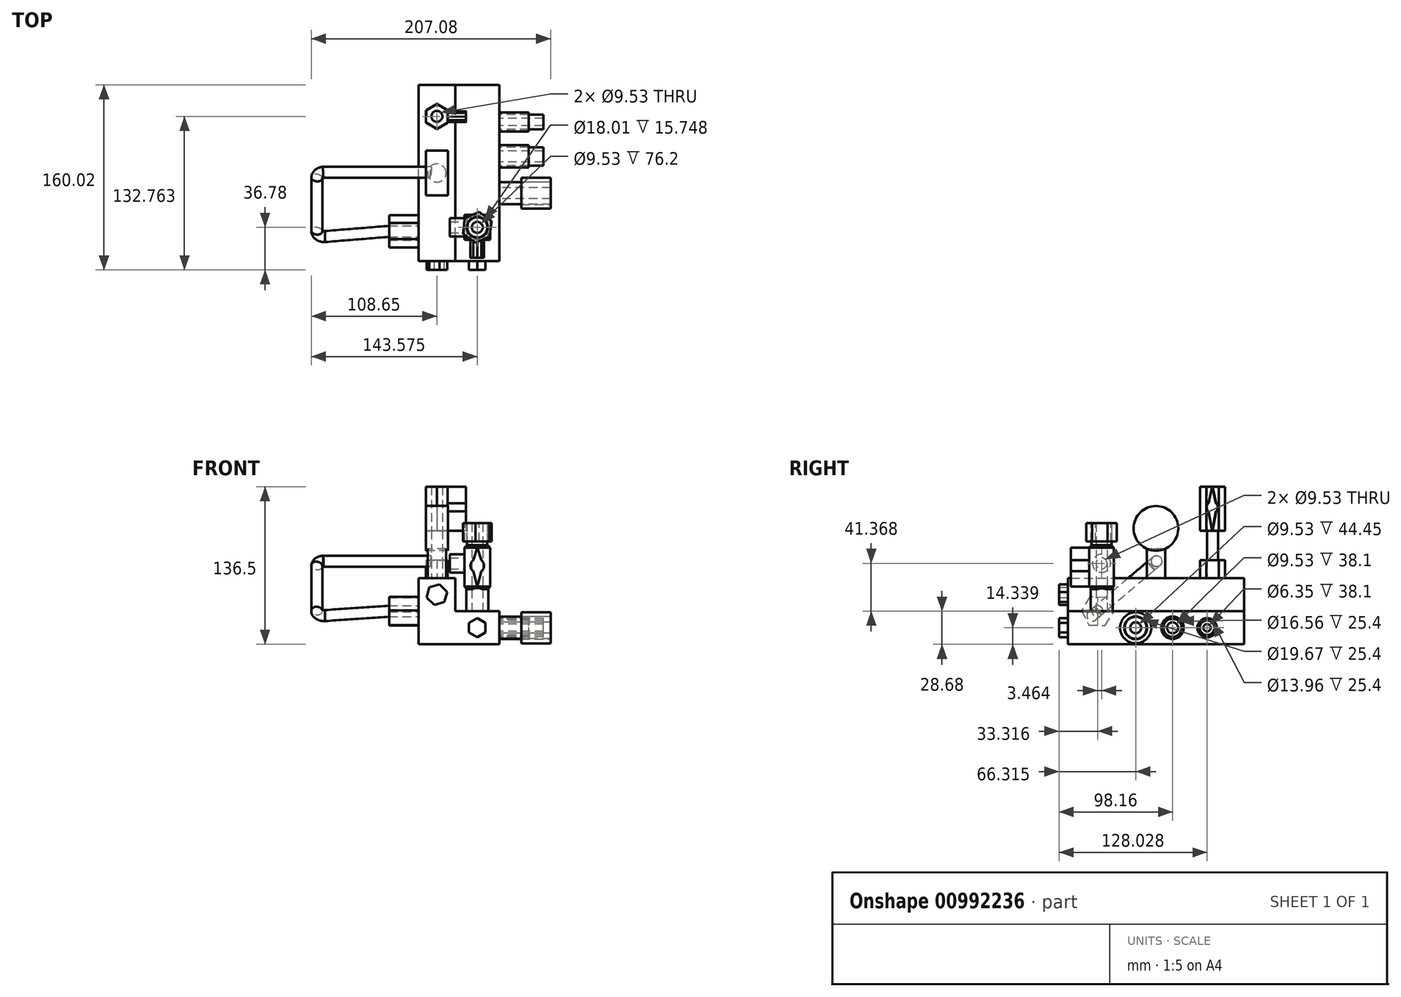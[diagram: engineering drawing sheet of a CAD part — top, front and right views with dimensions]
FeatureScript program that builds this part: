
annotation { "Feature Type Name" : "Feature", "Feature Type Description" : "" }
export const myFeature = defineFeature(function(context is Context, id is Id, definition is map)
    precondition{}
    {
        {
            var Q0;
            Q0=qCreatedBy(makeId("Front.planeOp"),FACE);
            var sketch = newSketch(context, id + "F0", { "sketchPlane" : qUnion([Q0])});
            skLineSegment(sketch, "E0.bottom", {"start": v(15.87, -28.57) * mm, "end": v(-15.88, -28.58) * mm});
            skLineSegment(sketch, "E0.top", {"start": v(15.88, 28.58) * mm, "end": v(-15.88, 28.57) * mm});
            skLineSegment(sketch, "E0.left", {"start": v(15.87, 0) * mm, "end": v(15.88, 28.58) * mm});
            skLineSegment(sketch, "E0.right", {"start": v(-15.88, -28.58) * mm, "end": v(-15.88, 28.57) * mm});
            skPoint(sketch, "E0.middle", {"position": v(0, 0) * mm});
            skLineSegment(sketch, "E1.bottom", {"start": v(15.87, 0) * mm, "end": v(53.97, 0) * mm});
            skLineSegment(sketch, "E1.top", {"start": v(15.87, -28.68) * mm, "end": v(53.97, -28.68) * mm});
            skLineSegment(sketch, "E1.left", {"start": v(15.87, -28.58) * mm, "end": v(15.87, -28.68) * mm});
            skLineSegment(sketch, "E1.right", {"start": v(53.97, 0) * mm, "end": v(53.97, -28.68) * mm});
            skSolve(sketch);
        }
        {
            var Q0;
            Q0 = qSketchRegion(id + "F0", true);
            extrude(context, id + "F1", {"entities" : qUnion([Q0]), "endBound" : BoundingType.SYMMETRIC, "depth" : 152.4 * mm, "offsetDistance" : 25.4 * mm});
        }
        {
            var Q0;
            Q0=makeQuery(id+"F1.opExtrude","SWEPT_FACE",FACE,{"disambiguationData":[OSD([sQuery(id+"F0.wireOp",EDGE,"E1.right")])]});
            var sketch = newSketch(context, id + "F2", { "sketchPlane" : qUnion([Q0])});
            skCircle(sketch, "E2", {"center": v(-17.5, -14.34) * mm, "radius": 9.53 * mm});
            skPoint(sketch, "E2.centerSnap0", {"position": v(-76.2, -14.34) * mm});
            skCircle(sketch, "E3", {"center": v(-17.5, -14.34) * mm, "radius": 4.76 * mm});
            skSolve(sketch);
        }
        {
            var Q0;
            Q0 = qSketchRegion(id + "F2", true);
            extrude(context, id + "F3", {"entities" : qUnion([Q0]), "operationType" : NewBodyOperationType.ADD, "depth" : 44.45 * mm, "offsetDistance" : 25.4 * mm});
        }
        {
            var Q0;
            {var subQ1=sQuery(id+"F0.wireOp",EDGE,"E1.right");var subQ3=sQuery(id+"F0.wireOp",EDGE,"E1.bottom");Q0=makeQuery(id+"F3.boolean.opBoolean","SPLIT",FACE,{"disambiguationData":[TD([makeQuery(id+"F1.opExtrude","SWEPT_FACE",FACE,{"disambiguationData":[OSD([subQ3])]})])],"derivedFrom":makeQuery(id+"F1.opExtrude","SWEPT_FACE",FACE,{"disambiguationData":[OSD([subQ1])]})});}
            var sketch = newSketch(context, id + "F4", { "sketchPlane" : qUnion([Q0])});
            skCircle(sketch, "E4", {"center": v(14.34, -14.34) * mm, "radius": 7.87 * mm});
            skPoint(sketch, "E4.centerSnap0", {"position": v(-76.2, -14.34) * mm});
            skCircle(sketch, "E5", {"center": v(14.34, -14.34) * mm, "radius": 4.76 * mm});
            skCircle(sketch, "E6", {"center": v(44.2, -14.34) * mm, "radius": 6.35 * mm});
            skCircle(sketch, "E7", {"center": v(44.2, -14.34) * mm, "radius": 3.18 * mm});
            skSolve(sketch);
        }
        {
            var Q0;
            Q0 = qSketchRegion(id + "F4", true);
            extrude(context, id + "F5", {"entities" : qUnion([Q0]), "operationType" : NewBodyOperationType.ADD, "depth" : 38.1 * mm, "offsetDistance" : 25.4 * mm});
        }
        {
            var Q0;
            Q0=makeQuery(id+"F3.opExtrude","CAP_FACE",FACE,{"disambiguationData":[OSD([sQuery(id+"F2.wireOp",EDGE,"E2"),sQuery(id+"F2.wireOp",EDGE,"E3")])],"isStart":false});
            var sketch = newSketch(context, id + "F6", { "sketchPlane" : qUnion([Q0])});
            skCircle(sketch, "E8", {"center": v(-17.5, -14.34) * mm, "radius": 9.84 * mm});
            skCircle(sketch, "E9", {"center": v(-17.5, -14.34) * mm, "radius": 13.46 * mm});
            skSolve(sketch);
        }
        {
            var Q0;
            Q0 = qSketchRegion(id + "F6", true);
            extrude(context, id + "F7", {"entities" : qUnion([Q0]), "oppositeDirection" : true, "depth" : 25.4 * mm, "offsetDistance" : 25.4 * mm});
        }
        {
            var Q0;
            {var subQ2=sQuery(id+"F0.wireOp",EDGE,"E1.right");var subQ4=sQuery(id+"F0.wireOp",EDGE,"E1.bottom");var subQ10=makeQuery(id+"F1.opExtrude","SWEPT_FACE",FACE,{"disambiguationData":[OSD([subQ4])]});Q0=makeQuery(id+"F5.boolean.opBoolean","SPLIT",FACE,{"disambiguationData":[TD([subQ10])],"derivedFrom":makeQuery(id+"F3.boolean.opBoolean","SPLIT",FACE,{"disambiguationData":[TD([subQ10])],"derivedFrom":makeQuery(id+"F1.opExtrude","SWEPT_FACE",FACE,{"disambiguationData":[OSD([subQ2])]})})});}
            var sketch = newSketch(context, id + "F8", { "sketchPlane" : qUnion([Q0])});
            skCircle(sketch, "E10", {"center": v(14.34, -14.34) * mm, "radius": 8.28 * mm});
            skCircle(sketch, "E11", {"center": v(14.34, -14.34) * mm, "radius": 9.67 * mm});
            skCircle(sketch, "E12", {"center": v(44.2, -14.34) * mm, "radius": 6.98 * mm});
            skCircle(sketch, "E13", {"center": v(44.2, -14.34) * mm, "radius": 8.3 * mm});
            skSolve(sketch);
        }
        {
            var Q0;
            Q0 = qSketchRegion(id + "F8", true);
            extrude(context, id + "F9", {"entities" : qUnion([Q0]), "depth" : 25.4 * mm, "offsetDistance" : 25.4 * mm});
        }
        {
            var Q0;
            Q0=makeQuery(id+"F1.opExtrude","SWEPT_FACE",FACE,{"disambiguationData":[OSD([sQuery(id+"F0.wireOp",EDGE,"E1.bottom")])]});
            var sketch = newSketch(context, id + "F10", { "sketchPlane" : qUnion([Q0])});
            skCircle(sketch, "E14", {"center": v(34.92, -47.04) * mm, "radius": 9.53 * mm});
            skPoint(sketch, "E14.centerSnap0", {"position": v(34.92, -76.2) * mm});
            skCircle(sketch, "E15", {"center": v(34.92, -47.04) * mm, "radius": 4.76 * mm});
            skSolve(sketch);
        }
        {
            var Q0;
            Q0 = qSketchRegion(id + "F10", true);
            extrude(context, id + "F11", {"entities" : qUnion([Q0]), "operationType" : NewBodyOperationType.ADD, "depth" : 19.05 * mm, "offsetDistance" : 25.4 * mm});
        }
        {
            var Q0;
            Q0=makeQuery(id+"F11.opExtrude","CAP_FACE",FACE,{"disambiguationData":[OSD([sQuery(id+"F10.wireOp",EDGE,"E14"),sQuery(id+"F10.wireOp",EDGE,"E15")])],"isStart":false});
            var sketch = newSketch(context, id + "F12", { "sketchPlane" : qUnion([Q0])});
            skLineSegment(sketch, "E16.bottom", {"start": v(46.02, -57.76) * mm, "end": v(23.83, -57.76) * mm});
            skLineSegment(sketch, "E16.top", {"start": v(46.02, -36.32) * mm, "end": v(23.83, -36.32) * mm});
            skLineSegment(sketch, "E16.left", {"start": v(46.02, -57.76) * mm, "end": v(46.02, -36.32) * mm});
            skLineSegment(sketch, "E16.right", {"start": v(23.83, -57.76) * mm, "end": v(23.83, -36.32) * mm});
            skPoint(sketch, "E16.middle", {"position": v(34.92, -47.04) * mm});
            skCircle(sketch, "E17", {"center": v(34.92, -47.04) * mm, "radius": 4.76 * mm});
            skSolve(sketch);
        }
        {
            var Q0;
            Q0 = qSketchRegion(id + "F12", true);
            extrude(context, id + "F13", {"entities" : qUnion([Q0]), "operationType" : NewBodyOperationType.ADD, "depth" : 38.1 * mm, "offsetDistance" : 25.4 * mm});
        }
        {
            var Q0;
            Q0=makeQuery(id+"F13.opExtrude","CAP_EDGE",EDGE,{"disambiguationData":[OSD([sQuery(id+"F12.wireOp",EDGE,"E16.right")])],"isStart":false});
            var Q1;
            Q1=makeQuery(id+"F13.opExtrude","CAP_EDGE",EDGE,{"disambiguationData":[OSD([sQuery(id+"F12.wireOp",EDGE,"E16.bottom")])],"isStart":false});
            var Q2;
            Q2=makeQuery(id+"F13.opExtrude","CAP_EDGE",EDGE,{"disambiguationData":[OSD([sQuery(id+"F12.wireOp",EDGE,"E16.left")])],"isStart":false});
            var Q3;
            Q3=makeQuery(id+"F13.opExtrude","CAP_EDGE",EDGE,{"disambiguationData":[OSD([sQuery(id+"F12.wireOp",EDGE,"E16.top")])],"isStart":false});
            var Q4;
            Q4=makeQuery(id+"F13.opExtrude","CAP_EDGE",EDGE,{"disambiguationData":[OSD([sQuery(id+"F12.wireOp",EDGE,"E16.bottom")])],"isStart":true});
            var Q5;
            Q5=makeQuery(id+"F13.opExtrude","CAP_EDGE",EDGE,{"disambiguationData":[OSD([sQuery(id+"F12.wireOp",EDGE,"E16.left")])],"isStart":true});
            var Q6;
            Q6=makeQuery(id+"F13.opExtrude","CAP_EDGE",EDGE,{"disambiguationData":[OSD([sQuery(id+"F12.wireOp",EDGE,"E16.top")])],"isStart":true});
            var Q7;
            Q7=makeQuery(id+"F13.opExtrude","CAP_EDGE",EDGE,{"disambiguationData":[OSD([sQuery(id+"F12.wireOp",EDGE,"E16.right")])],"isStart":true});
            chamfer(context, id + "F14", {"entities" : qUnion([Q0, Q1, Q2, Q3, Q4, Q5, Q6, Q7]), "width" : 2.3 * mm, "tangentPropagation" : true});
        }
        {
            var Q0;
            Q0=makeQuery(id+"F13.opExtrude","CAP_FACE",FACE,{"disambiguationData":[OSD([sQuery(id+"F12.wireOp",EDGE,"E16.bottom"),sQuery(id+"F12.wireOp",EDGE,"E16.top"),sQuery(id+"F12.wireOp",EDGE,"E16.left"),sQuery(id+"F12.wireOp",EDGE,"E16.right"),sQuery(id+"F12.wireOp",EDGE,"E17")])],"isStart":false});
            var sketch = newSketch(context, id + "F15", { "sketchPlane" : qUnion([Q0])});
            skCircle(sketch, "E18", {"center": v(34.92, -47.04) * mm, "radius": 8.73 * mm});
            skCircle(sketch, "E19", {"center": v(34.92, -47.04) * mm, "radius": 4.76 * mm});
            skSolve(sketch);
        }
        {
            var Q0;
            Q0 = qSketchRegion(id + "F15", true);
            extrude(context, id + "F16", {"entities" : qUnion([Q0]), "operationType" : NewBodyOperationType.ADD, "depth" : 19.05 * mm, "offsetDistance" : 25.4 * mm});
        }
        {
            var Q0;
            Q0=makeQuery(id+"F16.opExtrude","CAP_FACE",FACE,{"disambiguationData":[OSD([sQuery(id+"F15.wireOp",EDGE,"E18"),sQuery(id+"F15.wireOp",EDGE,"E19")])],"isStart":false});
            var sketch = newSketch(context, id + "F17", { "sketchPlane" : qUnion([Q0])});
            skCircle(sketch, "E20", {"center": v(34.92, -47.04) * mm, "radius": 9 * mm});
            skCircle(sketch, "E21.cCircle", {"center": v(34.92, -47.04) * mm, "radius": 11.58 * mm, "construction": true});
            skLineSegment(sketch, "E21.0", {"start": v(47.24, -41.82) * mm, "end": v(45.6, -55.1) * mm});
            skLineSegment(sketch, "E21.1", {"start": v(45.6, -55.1) * mm, "end": v(33.28, -60.31) * mm});
            skLineSegment(sketch, "E21.2", {"start": v(33.28, -60.31) * mm, "end": v(22.6, -52.26) * mm});
            skLineSegment(sketch, "E21.3", {"start": v(22.6, -52.26) * mm, "end": v(24.25, -38.98) * mm});
            skLineSegment(sketch, "E21.4", {"start": v(24.25, -38.98) * mm, "end": v(36.57, -33.77) * mm});
            skLineSegment(sketch, "E21.5", {"start": v(36.57, -33.77) * mm, "end": v(47.24, -41.82) * mm});
            skPoint(sketch, "E21.0.midPoint", {"position": v(46.42, -48.46) * mm});
            skSolve(sketch);
        }
        {
            var Q0;
            Q0 = qSketchRegion(id + "F17", true);
            extrude(context, id + "F18", {"entities" : qUnion([Q0]), "oppositeDirection" : true, "depth" : 15.75 * mm, "offsetDistance" : 25.4 * mm});
        }
        {
            var Q0;
            Q0=makeQuery(id+"F13.opExtrude","SWEPT_FACE",FACE,{"disambiguationData":[OSD([sQuery(id+"F12.wireOp",EDGE,"E16.bottom")])]});
            var sketch = newSketch(context, id + "F19", { "sketchPlane" : qUnion([Q0])});
            skCircle(sketch, "E22", {"center": v(34.92, 39.36) * mm, "radius": 5.92 * mm});
            skPoint(sketch, "E22.centerSnap0", {"position": v(34.92, 54.86) * mm});
            skLineSegment(sketch, "E23", {"start": v(34.92, 54.86) * mm, "end": v(34.92, 21.34) * mm, "construction": true});
            skLineSegment(sketch, "E24", {"start": v(31.51, 44.2) * mm, "end": v(34.92, 54.86) * mm});
            skLineSegment(sketch, "E25", {"start": v(31.51, 34.52) * mm, "end": v(34.92, 21.34) * mm});
            skLineSegment(sketch, "E26.MirrorCS", {"start": v(38.34, 44.2) * mm, "end": v(34.92, 54.86) * mm});
            skLineSegment(sketch, "E27.MirrorCS", {"start": v(38.34, 34.52) * mm, "end": v(34.92, 21.34) * mm});
            skSolve(sketch);
        }
        {
            var Q0;
            Q0 = qSketchRegion(id + "F19", true);
            extrude(context, id + "F20", {"entities" : qUnion([Q0]), "depth" : 15.75 * mm, "offsetDistance" : 25.4 * mm});
        }
        {
            var Q0;
            Q0=makeQuery(id+"F1.opExtrude","CAP_FACE",FACE,{"disambiguationData":[OSD([sQuery(id+"F0.wireOp",EDGE,"E0.bottom"),sQuery(id+"F0.wireOp",EDGE,"E0.top"),sQuery(id+"F0.wireOp",EDGE,"E0.left"),sQuery(id+"F0.wireOp",EDGE,"E0.right"),sQuery(id+"F0.wireOp",EDGE,"E1.bottom"),sQuery(id+"F0.wireOp",EDGE,"E1.top"),sQuery(id+"F0.wireOp",EDGE,"E1.left"),sQuery(id+"F0.wireOp",EDGE,"E1.right")])],"isStart":false});
            var sketch = newSketch(context, id + "F21", { "sketchPlane" : qUnion([Q0])});
            skCircle(sketch, "E28.cCircle", {"center": v(34.92, -14.34) * mm, "radius": 7.14 * mm, "construction": true});
            skPoint(sketch, "E28.cCircle.centerSnap0", {"position": v(53.97, -14.34) * mm});
            skPoint(sketch, "E28.cCircle.centerSnap1", {"position": v(34.92, 0) * mm});
            skLineSegment(sketch, "E28.0", {"start": v(42.07, -10.22) * mm, "end": v(42.07, -18.46) * mm});
            skLineSegment(sketch, "E28.1", {"start": v(42.07, -18.46) * mm, "end": v(34.92, -22.59) * mm});
            skLineSegment(sketch, "E28.2", {"start": v(34.92, -22.59) * mm, "end": v(27.78, -18.46) * mm});
            skLineSegment(sketch, "E28.3", {"start": v(27.78, -18.46) * mm, "end": v(27.78, -10.22) * mm});
            skLineSegment(sketch, "E28.4", {"start": v(27.78, -10.22) * mm, "end": v(34.92, -6.1) * mm});
            skLineSegment(sketch, "E28.5", {"start": v(34.92, -6.1) * mm, "end": v(42.07, -10.22) * mm});
            skPoint(sketch, "E28.0.midPoint", {"position": v(42.07, -14.34) * mm});
            skCircle(sketch, "E29.cCircle", {"center": v(0, 14.29) * mm, "radius": 7.91 * mm, "construction": true});
            skPoint(sketch, "E29.cCircle.centerSnap0", {"position": v(15.87, 14.29) * mm});
            skPoint(sketch, "E29.cCircle.centerSnap1", {"position": v(0, 28.58) * mm});
            skLineSegment(sketch, "E29.0", {"start": v(8.82, 16.68) * mm, "end": v(6.48, 7.85) * mm});
            skLineSegment(sketch, "E29.1", {"start": v(6.48, 7.85) * mm, "end": v(-2.34, 5.45) * mm});
            skLineSegment(sketch, "E29.2", {"start": v(-2.34, 5.45) * mm, "end": v(-8.82, 11.9) * mm});
            skLineSegment(sketch, "E29.3", {"start": v(-8.82, 11.9) * mm, "end": v(-6.48, 20.73) * mm});
            skLineSegment(sketch, "E29.4", {"start": v(-6.48, 20.73) * mm, "end": v(2.34, 23.12) * mm});
            skLineSegment(sketch, "E29.5", {"start": v(2.34, 23.12) * mm, "end": v(8.82, 16.68) * mm});
            skPoint(sketch, "E29.0.midPoint", {"position": v(7.65, 12.26) * mm});
            skSolve(sketch);
        }
        {
            var Q0;
            Q0 = qSketchRegion(id + "F21", true);
            extrude(context, id + "F22", {"entities" : qUnion([Q0]), "depth" : 7.62 * mm, "offsetDistance" : 25.4 * mm});
        }
        {
            var Q0;
            Q0=makeQuery(id+"F1.opExtrude","SWEPT_FACE",FACE,{"disambiguationData":[OSD([sQuery(id+"F0.wireOp",EDGE,"E0.top")])]});
            var sketch = newSketch(context, id + "F23", { "sketchPlane" : qUnion([Q0])});
            skCircle(sketch, "E30", {"center": v(0, 0) * mm, "radius": 7.87 * mm});
            skSolve(sketch);
        }
        {
            var Q0;
            Q0 = qSketchRegion(id + "F23", true);
            extrude(context, id + "F24", {"entities" : qUnion([Q0]), "depth" : 25.4 * mm, "offsetDistance" : 25.4 * mm});
        }
        {
            var Q0;
            Q0=qCreatedBy(makeId("Right.planeOp"),FACE);
            var sketch = newSketch(context, id + "F25", { "sketchPlane" : qUnion([Q0])});
            skCircle(sketch, "E31", {"center": v(0, 71.65) * mm, "radius": 19.36 * mm});
            skSolve(sketch);
        }
        {
            var Q0;
            Q0 = qSketchRegion(id + "F25", true);
            extrude(context, id + "F26", {"entities" : qUnion([Q0]), "endBound" : BoundingType.SYMMETRIC, "depth" : 19.05 * mm, "offsetDistance" : 25.4 * mm});
        }
        {
            var Q0;
            Q0=makeQuery(id+"F1.opExtrude","SWEPT_FACE",FACE,{"disambiguationData":[OSD([sQuery(id+"F0.wireOp",EDGE,"E0.top")])]});
            var sketch = newSketch(context, id + "F27", { "sketchPlane" : qUnion([Q0])});
            skCircle(sketch, "E32.cCircle", {"center": v(0, 48.94) * mm, "radius": 9.35 * mm, "construction": true});
            skLineSegment(sketch, "E32.0", {"start": v(9.35, 54.34) * mm, "end": v(9.35, 43.55) * mm});
            skLineSegment(sketch, "E32.1", {"start": v(9.35, 43.55) * mm, "end": v(0, 38.15) * mm});
            skLineSegment(sketch, "E32.2", {"start": v(0, 38.15) * mm, "end": v(-9.35, 43.55) * mm});
            skLineSegment(sketch, "E32.3", {"start": v(-9.35, 43.55) * mm, "end": v(-9.35, 54.34) * mm});
            skLineSegment(sketch, "E32.4", {"start": v(-9.35, 54.34) * mm, "end": v(0, 59.74) * mm});
            skLineSegment(sketch, "E32.5", {"start": v(0, 59.74) * mm, "end": v(9.35, 54.34) * mm});
            skPoint(sketch, "E32.0.midPoint", {"position": v(9.35, 48.94) * mm});
            skCircle(sketch, "E33", {"center": v(0, 48.94) * mm, "radius": 4.76 * mm});
            skSolve(sketch);
        }
        {
            var Q0;
            Q0 = qSketchRegion(id + "F27", true);
            extrude(context, id + "F28", {"entities" : qUnion([Q0]), "depth" : 15.75 * mm, "offsetDistance" : 25.4 * mm});
        }
        {
            var Q0;
            Q0=makeQuery(id+"F28.opExtrude","CAP_FACE",FACE,{"disambiguationData":[OSD([sQuery(id+"F27.wireOp",EDGE,"E32.0"),sQuery(id+"F27.wireOp",EDGE,"E32.1"),sQuery(id+"F27.wireOp",EDGE,"E32.2"),sQuery(id+"F27.wireOp",EDGE,"E32.3"),sQuery(id+"F27.wireOp",EDGE,"E32.4"),sQuery(id+"F27.wireOp",EDGE,"E32.5"),sQuery(id+"F27.wireOp",EDGE,"E33")])],"isStart":false});
            var sketch = newSketch(context, id + "F29", { "sketchPlane" : qUnion([Q0])});
            skCircle(sketch, "E34", {"center": v(0, 48.94) * mm, "radius": 4.76 * mm});
            skSolve(sketch);
        }
        {
            var Q0;
            Q0 = qSketchRegion(id + "F29", true);
            extrude(context, id + "F30", {"entities" : qUnion([Q0]), "depth" : 25.4 * mm, "offsetDistance" : 25.4 * mm});
        }
        {
            var Q0;
            Q0=makeQuery(id+"F30.opExtrude","CAP_FACE",FACE,{"disambiguationData":[OSD([sQuery(id+"F29.wireOp",EDGE,"E34")])],"isStart":false});
            var sketch = newSketch(context, id + "F31", { "sketchPlane" : qUnion([Q0])});
            skCircle(sketch, "E35.cCircle", {"center": v(0, 48.94) * mm, "radius": 9.3 * mm, "construction": true});
            skLineSegment(sketch, "E35.0", {"start": v(9.25, 43.48) * mm, "end": v(-0.1, 38.2) * mm});
            skLineSegment(sketch, "E35.1", {"start": v(-0.1, 38.2) * mm, "end": v(-9.35, 43.67) * mm});
            skLineSegment(sketch, "E35.2", {"start": v(-9.35, 43.67) * mm, "end": v(-9.25, 54.4) * mm});
            skLineSegment(sketch, "E35.3", {"start": v(-9.25, 54.4) * mm, "end": v(0.1, 59.68) * mm});
            skLineSegment(sketch, "E35.4", {"start": v(0.1, 59.68) * mm, "end": v(9.35, 54.22) * mm});
            skLineSegment(sketch, "E35.5", {"start": v(9.35, 54.22) * mm, "end": v(9.25, 43.48) * mm});
            skPoint(sketch, "E35.0.midPoint", {"position": v(4.57, 40.84) * mm});
            skCircle(sketch, "E36", {"center": v(0, 48.94) * mm, "radius": 4.76 * mm});
            skSolve(sketch);
        }
        {
            var Q0;
            Q0 = qSketchRegion(id + "F31", true);
            extrude(context, id + "F32", {"entities" : qUnion([Q0]), "depth" : 38.1 * mm, "offsetDistance" : 25.4 * mm});
        }
        {
            var Q0;
            Q0=makeQuery(id+"F32.opExtrude","SWEPT_FACE",FACE,{"disambiguationData":[OSD([sQuery(id+"F31.wireOp",EDGE,"E35.5")])]});
            var sketch = newSketch(context, id + "F33", { "sketchPlane" : qUnion([Q0])});
            skCircle(sketch, "E37", {"center": v(48.94, 89.85) * mm, "radius": 4.78 * mm});
            skPoint(sketch, "E37.centerSnap0", {"position": v(48.94, 107.82) * mm});
            skLineSegment(sketch, "E38", {"start": v(48.94, 107.82) * mm, "end": v(48.94, 69.72) * mm, "construction": true});
            skLineSegment(sketch, "E39", {"start": v(45.81, 93.47) * mm, "end": v(48.94, 107.82) * mm});
            skLineSegment(sketch, "E40", {"start": v(45.81, 86.24) * mm, "end": v(48.94, 69.72) * mm});
            skLineSegment(sketch, "E41.MirrorCS", {"start": v(52.07, 93.47) * mm, "end": v(48.94, 107.82) * mm});
            skLineSegment(sketch, "E42.MirrorCS", {"start": v(52.07, 86.24) * mm, "end": v(48.94, 69.72) * mm});
            skSolve(sketch);
        }
        {
            var Q0;
            Q0 = qSketchRegion(id + "F33", true);
            extrude(context, id + "F34", {"entities" : qUnion([Q0]), "depth" : 15.75 * mm, "offsetDistance" : 25.4 * mm});
        }
        {
            var Q0;
            Q0=makeQuery(id+"F1.opExtrude","SWEPT_FACE",FACE,{"disambiguationData":[OSD([sQuery(id+"F0.wireOp",EDGE,"E0.right")])]});
            var sketch = newSketch(context, id + "F35", { "sketchPlane" : qUnion([Q0])});
            skCircle(sketch, "E43.cCircle", {"center": v(50.5, 0) * mm, "radius": 12.16 * mm, "construction": true});
            skLineSegment(sketch, "E43.0", {"start": v(64.53, 0.52) * mm, "end": v(57.97, -11.89) * mm});
            skLineSegment(sketch, "E43.1", {"start": v(57.97, -11.89) * mm, "end": v(43.94, -12.41) * mm});
            skLineSegment(sketch, "E43.2", {"start": v(43.94, -12.41) * mm, "end": v(36.47, -0.52) * mm});
            skLineSegment(sketch, "E43.3", {"start": v(36.47, -0.52) * mm, "end": v(43.04, 11.89) * mm});
            skLineSegment(sketch, "E43.4", {"start": v(43.04, 11.89) * mm, "end": v(57.07, 12.41) * mm});
            skLineSegment(sketch, "E43.5", {"start": v(57.07, 12.41) * mm, "end": v(64.53, 0.52) * mm});
            skPoint(sketch, "E43.0.midPoint", {"position": v(61.25, -5.68) * mm});
            skCircle(sketch, "E44", {"center": v(50.5, 0) * mm, "radius": 4.76 * mm});
            skSolve(sketch);
        }
        {
            var Q0;
            Q0 = qSketchRegion(id + "F35", true);
            extrude(context, id + "F36", {"entities" : qUnion([Q0]), "depth" : 25.4 * mm, "offsetDistance" : 25.4 * mm});
        }
        {
            var Q0;
            Q0=makeQuery(id+"F36.opExtrude","CAP_FACE",FACE,{"disambiguationData":[OSD([sQuery(id+"F35.wireOp",EDGE,"E43.0"),sQuery(id+"F35.wireOp",EDGE,"E43.1"),sQuery(id+"F35.wireOp",EDGE,"E43.2"),sQuery(id+"F35.wireOp",EDGE,"E43.3"),sQuery(id+"F35.wireOp",EDGE,"E43.4"),sQuery(id+"F35.wireOp",EDGE,"E43.5"),sQuery(id+"F35.wireOp",EDGE,"E44")])],"isStart":false});
            var sketch = newSketch(context, id + "F37", { "sketchPlane" : qUnion([Q0])});
            skPoint(sketch, "E45.center.orphan", {"position": v(50.5, 0) * mm});
            skPoint(sketch, "E46", {"position": v(0, 42.8) * mm});
            skLineSegment(sketch, "E47", {"start": v(0, 42.8) * mm, "end": v(50.5, 0) * mm, "construction": true});
            skSolve(sketch);
        }
        {
            var Q0;
            Q0=sQuery(id+"F37.wireOp",EDGE,"E47");
            cPlane(context, id + "F38", {"entities" : qUnion([Q0]), "cplaneType" : CPlaneType.LINE_ANGLE, "offset" : 25.4 * mm, "angle" : 0 * degree, "width" : 152.4 * mm, "height" : 152.4 * mm});
        }
        {
            var Q0;
            Q0=qCreatedBy(id+"F38.planeOp",FACE);
            var sketch = newSketch(context, id + "F39", { "sketchPlane" : qUnion([Q0])});
            skLineSegment(sketch, "E48", {"start": v(-41.18, 38.57) * mm, "end": v(-96.94, 44.45) * mm});
            skLineSegment(sketch, "E49", {"start": v(-103.95, 38.13) * mm, "end": v(-103.95, -22.2) * mm});
            skPoint(sketch, "E50.visualSharp", {"position": v(-103.95, 45.18) * mm});
            skArc(sketch, "E50.filletArc", {"start": v(-96.94, 44.45) * mm, "mid": v(-101.85, 42.85) * mm, "end": v(-103.95, 38.13) * mm});
            skPoint(sketch, "E51.visualSharp", {"position": v(-103.95, -27.92) * mm});
            skArc(sketch, "E51.filletArc", {"start": v(-103.95, -22.2) * mm, "mid": v(-102.32, -26.45) * mm, "end": v(-98.27, -28.52) * mm});
            skPoint(sketch, "E52.end.orphan", {"position": v(0, -38.88) * mm});
            skLineSegment(sketch, "E53", {"start": v(-98.27, -28.52) * mm, "end": v(-5.32, -28.52) * mm});
            skSolve(sketch);
        }
        {
            var Q0;
            Q0=makeQuery(id+"F37.imprint","IMPRINT",FACE,{"disambiguationData":[TD([[makeQuery(id+"F37.imprint","IMPRINT",EDGE,{"derivedFrom":makeQuery(id+"F36.opExtrude","CAP_EDGE",EDGE,{"disambiguationData":[OSD([sQuery(id+"F35.wireOp",EDGE,"E44")])],"isStart":false})}),1.0]])]});
            var Q1;
            Q1=sQuery(id+"F39.wireOp",EDGE,"E48");
            var Q2;
            Q2=sQuery(id+"F39.wireOp",EDGE,"E50.filletArc");
            var Q3;
            Q3=sQuery(id+"F39.wireOp",EDGE,"E49");
            var Q4;
            Q4=sQuery(id+"F39.wireOp",EDGE,"E51.filletArc");
            var Q5;
            Q5=sQuery(id+"F39.wireOp",EDGE,"E53");
            sweep(context, id + "F40", {"profiles" : qUnion([Q0]), "path" : qUnion([Q1, Q2, Q3, Q4, Q5])});
        }
        {
            var Q0;
            Q0=makeQuery(id+"F13.opExtrude","SWEPT_FACE",FACE,{"disambiguationData":[OSD([sQuery(id+"F12.wireOp",EDGE,"E16.right")])]});
            var sketch = newSketch(context, id + "F41", { "sketchPlane" : qUnion([Q0])});
            skCircle(sketch, "E54", {"center": v(47.04, 41.37) * mm, "radius": 7.87 * mm});
            skPoint(sketch, "E54.centerSnap0", {"position": v(47.04, 54.86) * mm});
            skCircle(sketch, "E55", {"center": v(47.04, 41.37) * mm, "radius": 4.76 * mm});
            skSolve(sketch);
        }
        {
            var Q0;
            Q0 = qSketchRegion(id + "F41", true);
            extrude(context, id + "F42", {"entities" : qUnion([Q0]), "depth" : 12.7 * mm, "offsetDistance" : 25.4 * mm});
        }
    });
